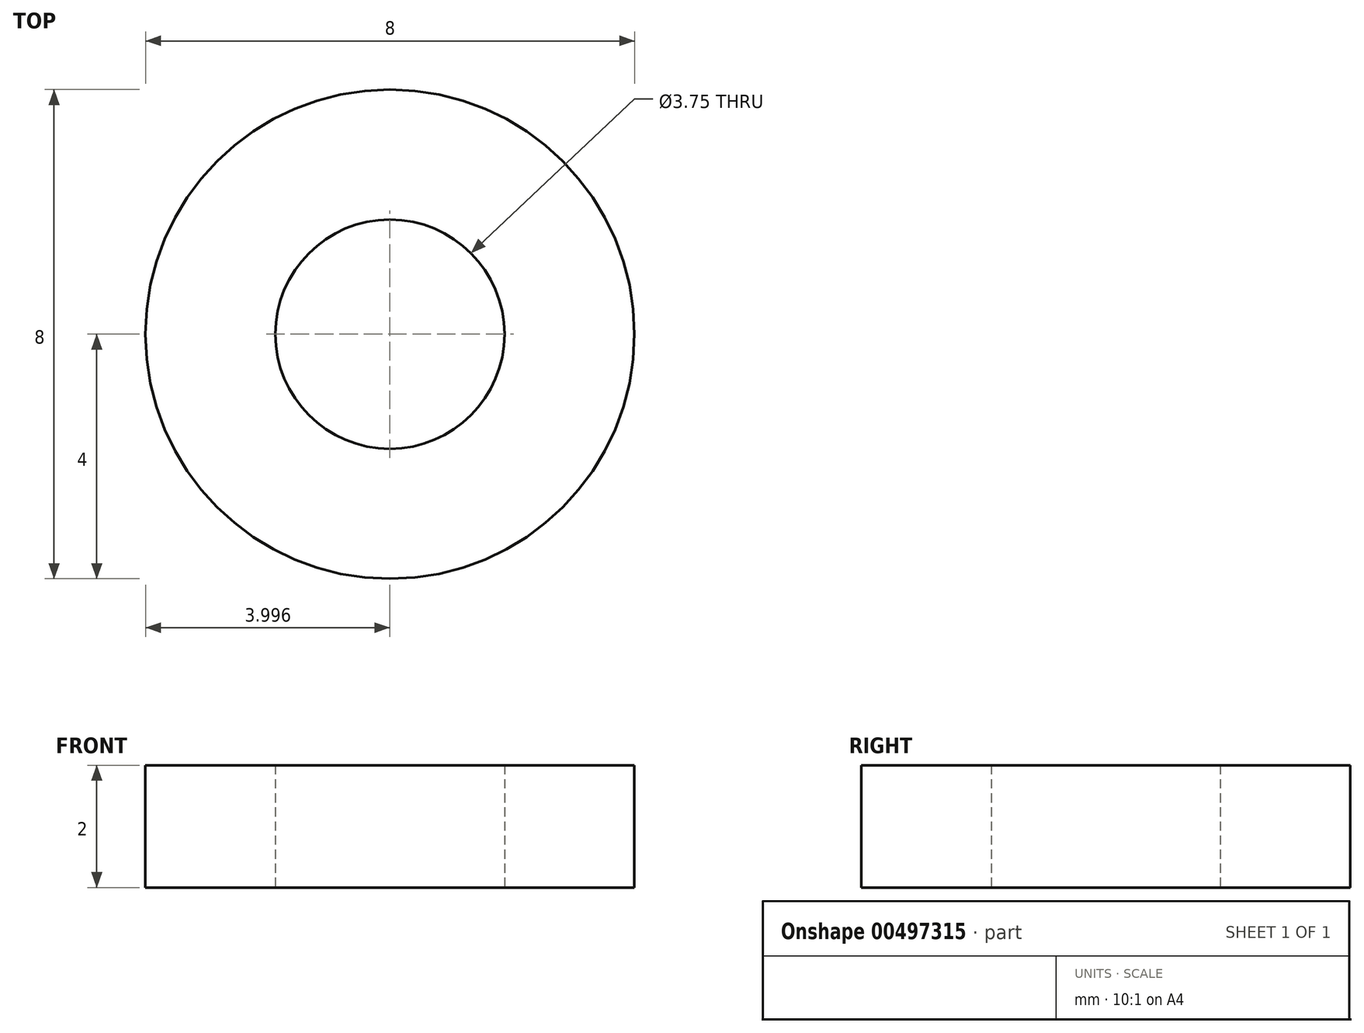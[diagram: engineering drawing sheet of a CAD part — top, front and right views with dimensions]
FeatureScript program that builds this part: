
annotation { "Feature Type Name" : "Feature", "Feature Type Description" : "" }
export const myFeature = defineFeature(function(context is Context, id is Id, definition is map)
    precondition{}
    {
        {
            var Q0;
            Q0=qCreatedBy(makeId("Top.planeOp"),FACE);
            var sketch = newSketch(context, id + "F0", { "sketchPlane" : qUnion([Q0])});
            skCircle(sketch, "E0", {"center": v(-34.96, 0) * mm, "radius": 4 * mm});
            skCircle(sketch, "E1", {"center": v(-34.96, 0) * mm, "radius": 1.88 * mm});
            skSolve(sketch);
        }
        {
            var Q0;
            Q0=makeQuery(id+"F0.imprint","IMPRINT",FACE,{"disambiguationData":[TD([[makeQuery(id+"F0.imprint","IMPRINT",EDGE,{"derivedFrom":sQuery(id+"F0.wireOp",EDGE,"E0")}),1.0]])]});
            extrude(context, id + "F1", {"entities" : qUnion([Q0]), "depth" : 2 * mm});
        }
    });
